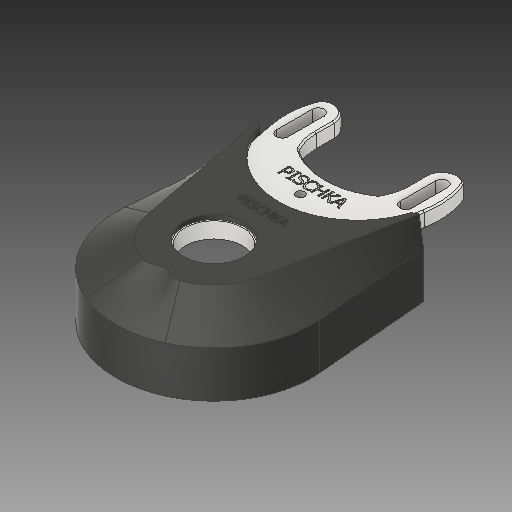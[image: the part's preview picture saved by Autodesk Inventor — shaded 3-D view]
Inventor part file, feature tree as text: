
AUTODESK INVENTOR PART (.ipt)
format: ipt  version: 2019.4 (Build 234330000, 330)  size: 1,453,056 bytes
history: native  units: mm
features: other x17, sketch x6, loft x6, extrude x5, plane x2, chamfer x2, mirror x1, emboss x1
ambient origin geometry x8: Origin, YZ Plane, XZ Plane, XY Plane, X Axis, Y Axis, Z Axis, Center Point
bodies: Body1 (feature_tree), Body2 (feature_tree)
feature tree (40):
  other  "Motor Holder v3 - 225 - ABS.ipt"
  plane  "Work Plane2"
  sketch  "Sketch2"  dims[d0=10.0mm d3=3.5mm]
  plane  "Work Plane1"
  extrude  "Extrusion4"  Depth=3.5mm
  sketch  "3D Sketch1"
  loft  "Loft6"
  extrude  "Extrusion5"  Depth=2.75mm
  extrude  "Extrusion6"  Depth=64.0mm
  loft  "Loft7"
  loft  "Loft8"
  loft  "Loft9"
  loft  "Loft10"
  loft  "Loft11"
  chamfer  "Chamfer3"  Distance=2.0mm
  extrude  "Extrusion7"  Depth=5.0mm TaperAngle=0.0deg
  chamfer  "Chamfer4"  Distance=1.5mm
  extrude  "Extrusion24"  Depth=16.0mm TaperAngle=0.0deg
  mirror  "Mirror2"
  emboss  "Emboss1"
  other  "Solid3::Motor Holder v3 - 225 - ABS.ipt"
  other  "TaggingFeature1"
  other  "Holder Cover"
  other  "Edges1"
  other  "Edges2"
  other  "Edges3"
  other  "Edges4"
  other  "Edges5"
  other  "Edges6"
  other  "Edges7"
  other  "Edges8"
  other  "Edges9"
  sketch  "3D Sketch2"
  sketch  "Sketch8"  dims[d4=3.5mm d5=21.0mm]
  sketch  "Sketch24"  dims[d6=2.5mm d14=2.75mm d15=2.75mm]
  sketch  "Sketch28"  dims[d24=-7.25mm d26=64.0mm d28=32.0mm d29=1.5mm d41=0.5mm d43=0.5mm d51=2.0mm d52=2.0mm d67=5.0mm d68=0.0mm d73=1.5mm d74=0.0mm d75=16.0mm d76=0.0mm d81=29.698599mm d88=0.858664mm d91=1.296614mm d92=45.0deg d97=3.5mm d100=3.5mm d103=0.0mm d104=90.0deg d105=0.0mm d106=90.0deg d107=0.0mm d108=90.0deg d109=0.0mm d110=90.0deg d111=0.0mm d112=90.0deg d113=0.0mm d114=90.0deg d115=0.0mm d116=90.0deg d117=0.0mm d118=90.0deg d119=0.0mm d120=90.0deg d121=0.0mm d122=90.0deg d123=0.0mm d124=90.0deg d125=0.0mm d126=90.0deg d127=0.5mm d128=1.5mm d129=45.0deg d130=23.0mm d131=0.0mm d132=0.5mm d133=1.5mm d134=45.0deg d146=2.75mm d170=52.0mm d171=2.0mm d264=2.0mm d267=2.0mm d294=1.452114mm d295=1.452114mm d304=1.452114mm d305=1.452114mm d329=15.0mm d330=0.0mm d331=5.0mm d332=5.0mm d333=5.0mm d334=30.0mm d335=0.5mm d336=0.0mm d337=0.0mm d338=90.0deg d339=0.0mm d340=90.0deg]
  other  "Edges10"
  other  "Edges11"
  other  "Edges12"
  other  "Holder"
